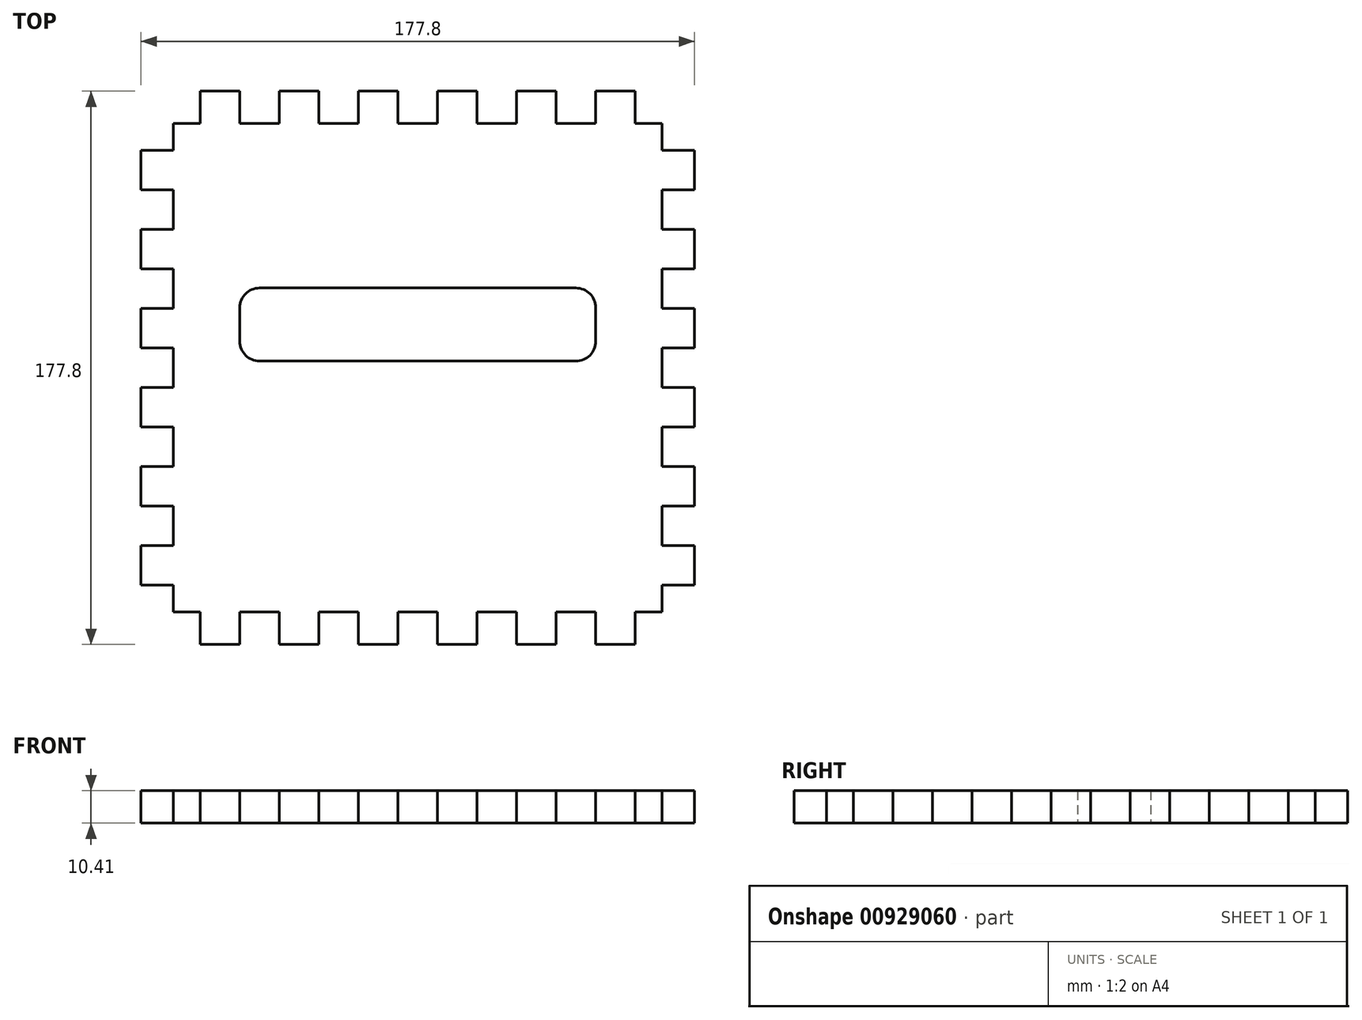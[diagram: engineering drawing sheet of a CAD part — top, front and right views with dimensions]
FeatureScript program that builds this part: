
annotation { "Feature Type Name" : "Feature", "Feature Type Description" : "" }
export const myFeature = defineFeature(function(context is Context, id is Id, definition is map)
    precondition{}
    {
        {
            var Q0;
            Q0=qCreatedBy(makeId("Top.planeOp"),FACE);
            var sketch = newSketch(context, id + "F0", { "sketchPlane" : qUnion([Q0])});
            skLineSegment(sketch, "E0.bottom", {"start": v(19.05, 0) * mm, "end": v(31.75, 0) * mm});
            skLineSegment(sketch, "E0.left", {"start": v(0, -19.05) * mm, "end": v(0, -31.75) * mm});
            skLineSegment(sketch, "E1", {"start": v(0, -19.05) * mm, "end": v(10.41, -19.05) * mm});
            skLineSegment(sketch, "E2", {"start": v(10.41, -19.05) * mm, "end": v(10.41, -10.41) * mm});
            skLineSegment(sketch, "E3", {"start": v(10.41, -10.41) * mm, "end": v(19.05, -10.41) * mm});
            skLineSegment(sketch, "E4", {"start": v(19.05, -10.41) * mm, "end": v(19.05, 0) * mm});
            skPoint(sketch, "E5.orphan", {"position": v(0, 0) * mm});
            skLineSegment(sketch, "E6", {"start": v(31.75, 0) * mm, "end": v(31.75, -10.41) * mm});
            skLineSegment(sketch, "E7", {"start": v(31.75, -10.41) * mm, "end": v(44.45, -10.41) * mm});
            skLineSegment(sketch, "E8", {"start": v(44.45, -10.41) * mm, "end": v(44.45, 0) * mm});
            skLineSegment(sketch, "E9", {"start": v(44.45, 0) * mm, "end": v(57.15, 0) * mm});
            skLineSegment(sketch, "E10", {"start": v(57.15, 0) * mm, "end": v(57.15, -10.41) * mm});
            skLineSegment(sketch, "E11", {"start": v(57.15, -10.41) * mm, "end": v(69.85, -10.41) * mm});
            skLineSegment(sketch, "E12", {"start": v(69.85, -10.41) * mm, "end": v(69.85, 0) * mm});
            skLineSegment(sketch, "E13", {"start": v(69.85, 0) * mm, "end": v(82.55, 0) * mm});
            skLineSegment(sketch, "E14", {"start": v(82.55, 0) * mm, "end": v(82.55, -10.41) * mm});
            skLineSegment(sketch, "E15", {"start": v(82.55, -10.41) * mm, "end": v(95.25, -10.41) * mm});
            skLineSegment(sketch, "E16", {"start": v(95.25, -10.41) * mm, "end": v(95.25, 0) * mm});
            skLineSegment(sketch, "E17.trimOffspring", {"start": v(95.25, 0) * mm, "end": v(107.95, 0) * mm});
            skLineSegment(sketch, "E18", {"start": v(107.95, 0) * mm, "end": v(107.95, -10.41) * mm});
            skLineSegment(sketch, "E19", {"start": v(107.95, -10.41) * mm, "end": v(120.65, -10.41) * mm});
            skLineSegment(sketch, "E20", {"start": v(120.65, -10.41) * mm, "end": v(120.65, 0) * mm});
            skLineSegment(sketch, "E21", {"start": v(120.65, 0) * mm, "end": v(133.35, 0) * mm});
            skLineSegment(sketch, "E22", {"start": v(133.35, 0) * mm, "end": v(133.35, -10.41) * mm});
            skLineSegment(sketch, "E23", {"start": v(133.35, -10.41) * mm, "end": v(146.05, -10.41) * mm});
            skLineSegment(sketch, "E24", {"start": v(146.05, -10.41) * mm, "end": v(146.05, 0) * mm});
            skLineSegment(sketch, "E25.trimOffspring", {"start": v(146.05, 0) * mm, "end": v(158.75, 0) * mm});
            skLineSegment(sketch, "E26", {"start": v(158.75, 0) * mm, "end": v(158.75, -10.41) * mm});
            skLineSegment(sketch, "E27", {"start": v(158.75, -10.41) * mm, "end": v(167.39, -10.41) * mm});
            skLineSegment(sketch, "E28", {"start": v(167.39, -10.41) * mm, "end": v(167.39, -19.05) * mm});
            skLineSegment(sketch, "E29", {"start": v(167.39, -19.05) * mm, "end": v(177.8, -19.05) * mm});
            skPoint(sketch, "E30.orphan", {"position": v(177.8, 0) * mm});
            skLineSegment(sketch, "E31", {"start": v(0, -31.75) * mm, "end": v(10.41, -31.75) * mm});
            skLineSegment(sketch, "E32", {"start": v(10.41, -31.75) * mm, "end": v(10.41, -44.45) * mm});
            skLineSegment(sketch, "E33", {"start": v(10.41, -44.45) * mm, "end": v(0, -44.45) * mm});
            skLineSegment(sketch, "E34", {"start": v(0, -44.45) * mm, "end": v(0, -57.15) * mm});
            skLineSegment(sketch, "E35", {"start": v(0, -57.15) * mm, "end": v(10.41, -57.15) * mm});
            skLineSegment(sketch, "E36", {"start": v(10.41, -57.15) * mm, "end": v(10.41, -69.85) * mm});
            skLineSegment(sketch, "E37", {"start": v(10.41, -69.85) * mm, "end": v(0, -69.85) * mm});
            skLineSegment(sketch, "E38", {"start": v(0, -69.85) * mm, "end": v(0, -82.55) * mm});
            skLineSegment(sketch, "E39", {"start": v(0, -82.55) * mm, "end": v(10.41, -82.55) * mm});
            skLineSegment(sketch, "E40", {"start": v(10.41, -82.55) * mm, "end": v(10.41, -95.25) * mm});
            skLineSegment(sketch, "E41", {"start": v(10.41, -95.25) * mm, "end": v(0, -95.25) * mm});
            skLineSegment(sketch, "E42.trimOffspring", {"start": v(0, -95.25) * mm, "end": v(0, -107.95) * mm});
            skLineSegment(sketch, "E43", {"start": v(0, -107.95) * mm, "end": v(10.41, -107.95) * mm});
            skLineSegment(sketch, "E44", {"start": v(10.41, -107.95) * mm, "end": v(10.41, -120.65) * mm});
            skLineSegment(sketch, "E45", {"start": v(10.41, -120.65) * mm, "end": v(0, -120.65) * mm});
            skLineSegment(sketch, "E46", {"start": v(0, -120.65) * mm, "end": v(0, -133.35) * mm});
            skLineSegment(sketch, "E47", {"start": v(0, -133.35) * mm, "end": v(10.41, -133.35) * mm});
            skLineSegment(sketch, "E48", {"start": v(10.41, -133.35) * mm, "end": v(10.41, -146.05) * mm});
            skLineSegment(sketch, "E49", {"start": v(10.41, -146.05) * mm, "end": v(0, -146.05) * mm});
            skLineSegment(sketch, "E50.trimOffspring", {"start": v(0, -146.05) * mm, "end": v(0, -158.75) * mm});
            skLineSegment(sketch, "E51", {"start": v(0, -158.75) * mm, "end": v(10.41, -158.75) * mm});
            skLineSegment(sketch, "E52", {"start": v(10.41, -158.75) * mm, "end": v(10.41, -167.39) * mm});
            skLineSegment(sketch, "E53", {"start": v(10.41, -167.39) * mm, "end": v(19.05, -167.39) * mm});
            skLineSegment(sketch, "E54", {"start": v(19.05, -167.39) * mm, "end": v(19.05, -177.8) * mm});
            skPoint(sketch, "E55.orphan", {"position": v(0, -177.8) * mm});
            skLineSegment(sketch, "E56", {"start": v(88.9, -10.41) * mm, "end": v(88.9, -10.41) * mm});
            skLineSegment(sketch, "E57", {"start": v(10.41, -88.9) * mm, "end": v(10.41, -88.9) * mm});
            skLineSegment(sketch, "E58.MirrorCS", {"start": v(177.8, -107.95) * mm, "end": v(167.39, -107.95) * mm});
            skLineSegment(sketch, "E59.MirrorCS", {"start": v(167.39, -120.65) * mm, "end": v(177.8, -120.65) * mm});
            skLineSegment(sketch, "E60.MirrorCS", {"start": v(167.39, -146.05) * mm, "end": v(177.8, -146.05) * mm});
            skLineSegment(sketch, "E61.MirrorCS", {"start": v(177.8, -133.35) * mm, "end": v(167.39, -133.35) * mm});
            skLineSegment(sketch, "E62.MirrorCS", {"start": v(177.8, -57.15) * mm, "end": v(167.39, -57.15) * mm});
            skLineSegment(sketch, "E63.MirrorCS", {"start": v(177.8, -19.05) * mm, "end": v(167.39, -19.05) * mm});
            skLineSegment(sketch, "E64.MirrorCS", {"start": v(167.39, -69.85) * mm, "end": v(177.8, -69.85) * mm});
            skLineSegment(sketch, "E65.MirrorCS", {"start": v(167.39, -44.45) * mm, "end": v(177.8, -44.45) * mm});
            skLineSegment(sketch, "E66.MirrorCS", {"start": v(167.39, -95.25) * mm, "end": v(177.8, -95.25) * mm});
            skLineSegment(sketch, "E67.MirrorCS", {"start": v(177.8, -158.75) * mm, "end": v(167.39, -158.75) * mm});
            skLineSegment(sketch, "E68.MirrorCS", {"start": v(177.8, -31.75) * mm, "end": v(167.39, -31.75) * mm});
            skLineSegment(sketch, "E69.MirrorCS", {"start": v(167.39, -167.39) * mm, "end": v(158.75, -167.39) * mm});
            skLineSegment(sketch, "E70.MirrorCS", {"start": v(167.39, -158.75) * mm, "end": v(167.39, -167.39) * mm});
            skLineSegment(sketch, "E71.MirrorCS", {"start": v(177.8, -82.55) * mm, "end": v(167.39, -82.55) * mm});
            skLineSegment(sketch, "E72.MirrorCS", {"start": v(177.8, -95.25) * mm, "end": v(177.8, -107.95) * mm});
            skLineSegment(sketch, "E73.MirrorCS", {"start": v(177.8, -146.05) * mm, "end": v(177.8, -158.75) * mm});
            skLineSegment(sketch, "E74.MirrorCS", {"start": v(177.8, -69.85) * mm, "end": v(177.8, -82.55) * mm});
            skLineSegment(sketch, "E75.MirrorCS", {"start": v(167.39, -82.55) * mm, "end": v(167.39, -95.25) * mm});
            skLineSegment(sketch, "E76.MirrorCS", {"start": v(177.8, -120.65) * mm, "end": v(177.8, -133.35) * mm});
            skLineSegment(sketch, "E77.MirrorCS", {"start": v(177.8, -19.05) * mm, "end": v(177.8, -31.75) * mm});
            skLineSegment(sketch, "E78.MirrorCS", {"start": v(177.8, -44.45) * mm, "end": v(177.8, -57.15) * mm});
            skLineSegment(sketch, "E79.MirrorCS", {"start": v(167.39, -133.35) * mm, "end": v(167.39, -146.05) * mm});
            skLineSegment(sketch, "E80.MirrorCS", {"start": v(167.39, -31.75) * mm, "end": v(167.39, -44.45) * mm});
            skLineSegment(sketch, "E81.MirrorCS", {"start": v(167.39, -57.15) * mm, "end": v(167.39, -69.85) * mm});
            skLineSegment(sketch, "E82.MirrorCS", {"start": v(167.39, -107.95) * mm, "end": v(167.39, -120.65) * mm});
            skLineSegment(sketch, "E83.MirrorCS", {"start": v(158.75, -167.39) * mm, "end": v(158.75, -177.8) * mm});
            skLineSegment(sketch, "E84.MirrorCS", {"start": v(146.05, -177.8) * mm, "end": v(158.75, -177.8) * mm});
            skLineSegment(sketch, "E85.MirrorCS", {"start": v(19.05, -177.8) * mm, "end": v(31.75, -177.8) * mm});
            skLineSegment(sketch, "E86.MirrorCS", {"start": v(120.65, -177.8) * mm, "end": v(133.35, -177.8) * mm});
            skLineSegment(sketch, "E87.MirrorCS", {"start": v(95.25, -177.8) * mm, "end": v(107.95, -177.8) * mm});
            skLineSegment(sketch, "E88.MirrorCS", {"start": v(69.85, -177.8) * mm, "end": v(82.55, -177.8) * mm});
            skLineSegment(sketch, "E89.MirrorCS", {"start": v(44.45, -177.8) * mm, "end": v(57.15, -177.8) * mm});
            skLineSegment(sketch, "E90.MirrorCS", {"start": v(57.15, -167.39) * mm, "end": v(69.85, -167.39) * mm});
            skLineSegment(sketch, "E91.MirrorCS", {"start": v(158.75, -167.39) * mm, "end": v(167.39, -167.39) * mm});
            skLineSegment(sketch, "E92.MirrorCS", {"start": v(107.95, -167.39) * mm, "end": v(120.65, -167.39) * mm});
            skLineSegment(sketch, "E93.MirrorCS", {"start": v(133.35, -167.39) * mm, "end": v(146.05, -167.39) * mm});
            skLineSegment(sketch, "E94.MirrorCS", {"start": v(31.75, -167.39) * mm, "end": v(44.45, -167.39) * mm});
            skLineSegment(sketch, "E95.MirrorCS", {"start": v(82.55, -167.39) * mm, "end": v(95.25, -167.39) * mm});
            skLineSegment(sketch, "E96.MirrorCS", {"start": v(146.05, -167.39) * mm, "end": v(146.05, -177.8) * mm});
            skLineSegment(sketch, "E97.MirrorCS", {"start": v(133.35, -177.8) * mm, "end": v(133.35, -167.39) * mm});
            skLineSegment(sketch, "E98.MirrorCS", {"start": v(120.65, -167.39) * mm, "end": v(120.65, -177.8) * mm});
            skLineSegment(sketch, "E99.MirrorCS", {"start": v(107.95, -177.8) * mm, "end": v(107.95, -167.39) * mm});
            skLineSegment(sketch, "E100.MirrorCS", {"start": v(95.25, -167.39) * mm, "end": v(95.25, -177.8) * mm});
            skLineSegment(sketch, "E101.MirrorCS", {"start": v(82.55, -177.8) * mm, "end": v(82.55, -167.39) * mm});
            skLineSegment(sketch, "E102.MirrorCS", {"start": v(69.85, -167.39) * mm, "end": v(69.85, -177.8) * mm});
            skLineSegment(sketch, "E103.MirrorCS", {"start": v(57.15, -177.8) * mm, "end": v(57.15, -167.39) * mm});
            skLineSegment(sketch, "E104.MirrorCS", {"start": v(44.45, -167.39) * mm, "end": v(44.45, -177.8) * mm});
            skLineSegment(sketch, "E105.MirrorCS", {"start": v(31.75, -177.8) * mm, "end": v(31.75, -167.39) * mm});
            skLineSegment(sketch, "E106.bottom", {"start": v(38.1, -63.25) * mm, "end": v(139.7, -63.25) * mm});
            skLineSegment(sketch, "E106.top", {"start": v(38.1, -86.74) * mm, "end": v(139.7, -86.74) * mm});
            skLineSegment(sketch, "E106.left", {"start": v(31.75, -69.6) * mm, "end": v(31.75, -80.4) * mm});
            skLineSegment(sketch, "E106.right", {"start": v(146.05, -69.6) * mm, "end": v(146.05, -80.4) * mm});
            skLineSegment(sketch, "E107", {"start": v(88.9, -10.41) * mm, "end": v(88.9, -63.25) * mm, "construction": true});
            skPoint(sketch, "E108.visualSharp", {"position": v(31.75, -63.25) * mm});
            skArc(sketch, "E108.filletArc", {"start": v(38.1, -63.25) * mm, "mid": v(33.6, -65.1) * mm, "end": v(31.75, -69.6) * mm});
            skPoint(sketch, "E109.visualSharp", {"position": v(31.75, -86.74) * mm});
            skArc(sketch, "E109.filletArc", {"start": v(31.75, -80.4) * mm, "mid": v(33.6, -84.88) * mm, "end": v(38.1, -86.74) * mm});
            skPoint(sketch, "E110.visualSharp", {"position": v(146.05, -63.25) * mm});
            skArc(sketch, "E110.filletArc", {"start": v(146.05, -69.6) * mm, "mid": v(144.2, -65.1) * mm, "end": v(139.7, -63.25) * mm});
            skPoint(sketch, "E111.visualSharp", {"position": v(146.05, -86.74) * mm});
            skArc(sketch, "E111.filletArc", {"start": v(139.7, -86.74) * mm, "mid": v(144.2, -84.88) * mm, "end": v(146.05, -80.4) * mm});
            skSolve(sketch);
        }
        {
            var Q0;
            Q0=makeQuery(id+"F0.imprint","IMPRINT",FACE,{"disambiguationData":[TD([[makeQuery(id+"F0.imprint","IMPRINT",EDGE,{"derivedFrom":sQuery(id+"F0.wireOp",EDGE,"E1")}),-1.0]])]});
            extrude(context, id + "F1", {"entities" : qUnion([Q0]), "depth" : 10.4 * mm, "offsetDistance" : 25.4 * mm});
        }
    });
